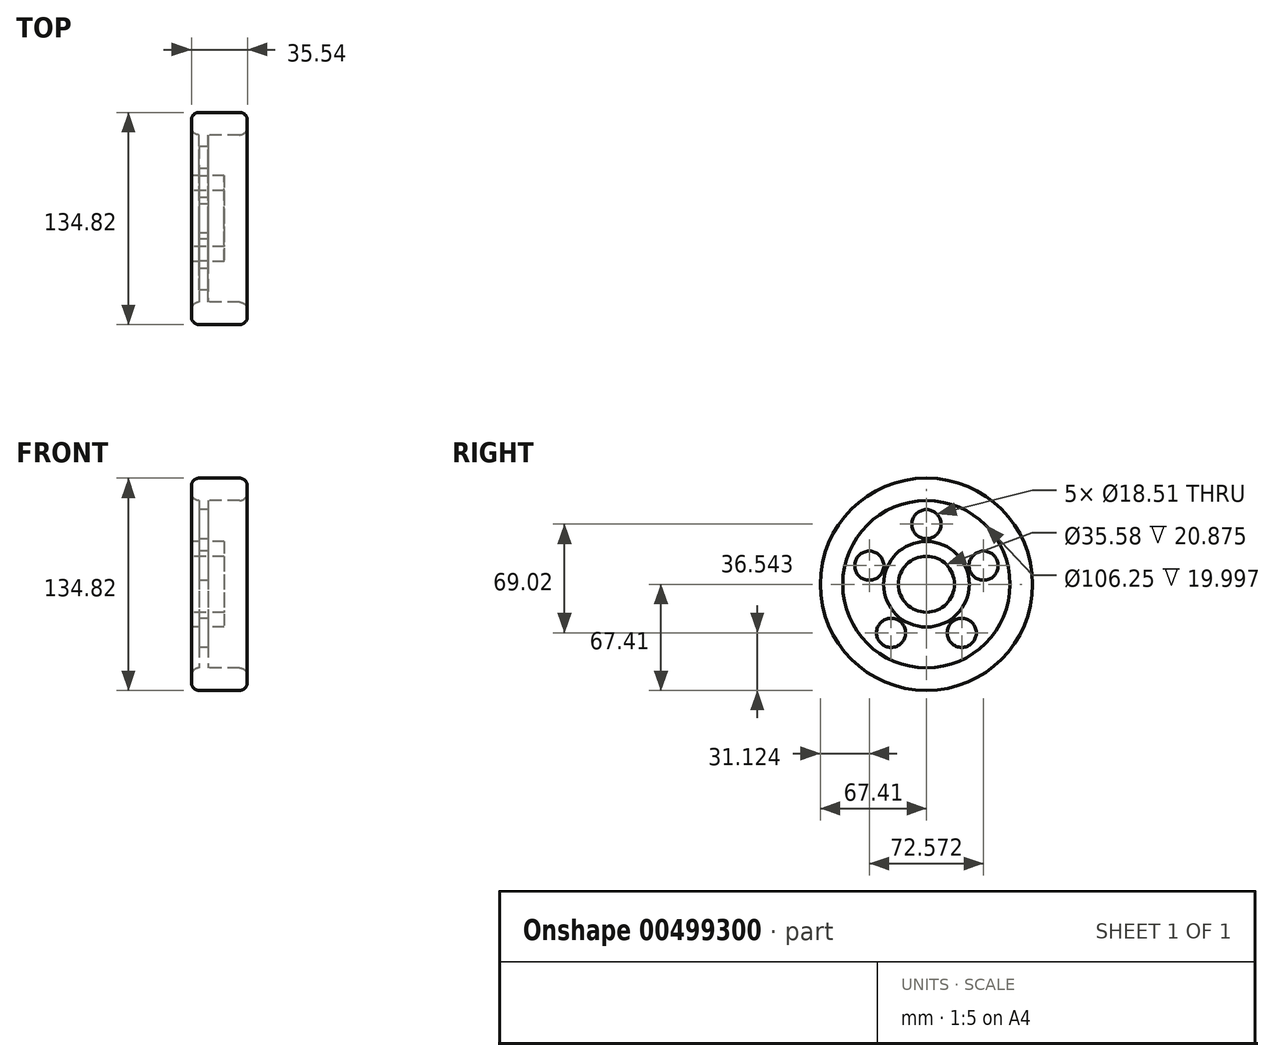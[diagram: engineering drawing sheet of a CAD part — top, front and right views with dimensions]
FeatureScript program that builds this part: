
annotation { "Feature Type Name" : "Feature", "Feature Type Description" : "" }
export const myFeature = defineFeature(function(context is Context, id is Id, definition is map)
    precondition{}
    {
        {
            var Q0;
            Q0=qCreatedBy(makeId("Front.planeOp"),FACE);
            var sketch = newSketch(context, id + "F0", { "sketchPlane" : qUnion([Q0])});
            skSolve(sketch);
        }
        {
            var Q0;
            Q0=qCreatedBy(makeId("Front.planeOp"),FACE);
            var sketch = newSketch(context, id + "F1", { "sketchPlane" : qUnion([Q0])});
            skLineSegment(sketch, "E0", {"start": v(0, 0) * mm, "end": v(17.87, 0) * mm});
            skLineSegment(sketch, "E1", {"start": v(0, 17.8) * mm, "end": v(20.88, 17.8) * mm});
            skLineSegment(sketch, "E2", {"start": v(20.88, 17.8) * mm, "end": v(20.88, 27.19) * mm});
            skLineSegment(sketch, "E3", {"start": v(20.88, 27.19) * mm, "end": v(10.54, 27.19) * mm});
            skLineSegment(sketch, "E4", {"start": v(10.54, 27.19) * mm, "end": v(10.54, 53.12) * mm});
            skLineSegment(sketch, "E5", {"start": v(10.54, 53.12) * mm, "end": v(35.54, 53.12) * mm});
            skLineSegment(sketch, "E6", {"start": v(35.54, 53.12) * mm, "end": v(35.54, 67.4) * mm});
            skLineSegment(sketch, "E7", {"start": v(35.54, 67.4) * mm, "end": v(10.54, 67.4) * mm});
            skLineSegment(sketch, "E8", {"start": v(10.54, 67.4) * mm, "end": v(0, 67.4) * mm});
            skLineSegment(sketch, "E9", {"start": v(0, 65.72) * mm, "end": v(0, 53.12) * mm});
            skLineSegment(sketch, "E10", {"start": v(0, 67.4) * mm, "end": v(0, 65.72) * mm});
            skLineSegment(sketch, "E11", {"start": v(0, 53.12) * mm, "end": v(4.9, 53.12) * mm});
            skLineSegment(sketch, "E12", {"start": v(4.9, 53.12) * mm, "end": v(4.9, 27.19) * mm});
            skLineSegment(sketch, "E13", {"start": v(4.9, 27.19) * mm, "end": v(0, 27.19) * mm});
            skLineSegment(sketch, "E14", {"start": v(0, 27.19) * mm, "end": v(0, 17.8) * mm});
            skSolve(sketch);
        }
        {
            var Q0;
            Q0=makeQuery(id+"F1.imprint","IMPRINT",FACE,{"disambiguationData":[TD([[makeQuery(id+"F1.imprint","IMPRINT",EDGE,{"derivedFrom":sQuery(id+"F1.wireOp",EDGE,"E1")}),1.0]])]});
            var Q1;
            Q1 = qSketchRegion(id + "F0", true);
            var Q2;
            Q2=sQuery(id+"F1.wireOp",EDGE,"E0");
            revolve(context, id + "F2", {"entities" : qUnion([Q0, Q1]), "axis" : qUnion([Q2]), "revolveType" : RevolveType.FULL});
        }
        {
            var Q0;
            Q0=makeQuery(id+"F2.opRevolve","SWEPT_FACE",FACE,{"disambiguationData":[OSD([sQuery(id+"F1.wireOp",EDGE,"E12")])]});
            var sketch = newSketch(context, id + "F3", { "sketchPlane" : qUnion([Q0])});
            skCircle(sketch, "E15", {"center": v(0, 38.15) * mm, "radius": 9.26 * mm});
            skCircle(sketch, "E16.1.0", {"center": v(-36.29, 11.8) * mm, "radius": 9.26 * mm});
            skCircle(sketch, "E16.2.0", {"center": v(-22.43, -30.87) * mm, "radius": 9.26 * mm});
            skCircle(sketch, "E16.3.0", {"center": v(22.43, -30.87) * mm, "radius": 9.26 * mm});
            skCircle(sketch, "E16.4.0", {"center": v(36.29, 11.8) * mm, "radius": 9.26 * mm});
            skPoint(sketch, "E16.center", {"position": v(0, 0) * mm});
            skSolve(sketch);
        }
        {
            var Q0;
            Q0=makeQuery(id+"F3.imprint","IMPRINT",FACE,{"disambiguationData":[TD([[makeQuery(id+"F3.imprint","IMPRINT",EDGE,{"derivedFrom":sQuery(id+"F3.wireOp",EDGE,"E16.1.0")}),1.0]])]});
            var Q1;
            Q1=makeQuery(id+"F3.imprint","IMPRINT",FACE,{"disambiguationData":[TD([[makeQuery(id+"F3.imprint","IMPRINT",EDGE,{"derivedFrom":sQuery(id+"F3.wireOp",EDGE,"E15")}),1.0]])]});
            var Q2;
            Q2=makeQuery(id+"F3.imprint","IMPRINT",FACE,{"disambiguationData":[TD([[makeQuery(id+"F3.imprint","IMPRINT",EDGE,{"derivedFrom":sQuery(id+"F3.wireOp",EDGE,"E16.4.0")}),1.0]])]});
            var Q3;
            Q3=makeQuery(id+"F3.imprint","IMPRINT",FACE,{"disambiguationData":[TD([[makeQuery(id+"F3.imprint","IMPRINT",EDGE,{"derivedFrom":sQuery(id+"F3.wireOp",EDGE,"E16.2.0")}),1.0]])]});
            var Q4;
            Q4=makeQuery(id+"F3.imprint","IMPRINT",FACE,{"disambiguationData":[TD([[makeQuery(id+"F3.imprint","IMPRINT",EDGE,{"derivedFrom":sQuery(id+"F3.wireOp",EDGE,"E16.3.0")}),1.0]])]});
            extrude(context, id + "F4", {"entities" : qUnion([Q0, Q1, Q2, Q3, Q4]), "operationType" : NewBodyOperationType.REMOVE, "oppositeDirection" : true, "depth" : 25 * mm});
        }
        {
            var Q0;
            Q0=makeQuery(id+"F2.opRevolve","SWEPT_EDGE",EDGE,{"disambiguationData":[OSD([sQuery(id+"F1.wireOp",EDGE,"E8"),sQuery(id+"F1.wireOp",EDGE,"E10")])]});
            var Q1;
            Q1=makeQuery(id+"F2.opRevolve","SWEPT_EDGE",EDGE,{"disambiguationData":[OSD([sQuery(id+"F1.wireOp",EDGE,"E6"),sQuery(id+"F1.wireOp",EDGE,"E7")])]});
            var Q2;
            Q2=makeQuery(id+"F2.opRevolve","SWEPT_EDGE",EDGE,{"disambiguationData":[OSD([sQuery(id+"F1.wireOp",EDGE,"E5"),sQuery(id+"F1.wireOp",EDGE,"E6")])]});
            var Q3;
            Q3=makeQuery(id+"F2.opRevolve","SWEPT_EDGE",EDGE,{"disambiguationData":[OSD([sQuery(id+"F1.wireOp",EDGE,"E9"),sQuery(id+"F1.wireOp",EDGE,"E11")])]});
            fillet(context, id + "F5", {"entities" : qUnion([Q0, Q1, Q2, Q3]), "radius" : 5 * mm, "tangentPropagation" : true, "allowEdgeOverflow" : false});
        }
    });
